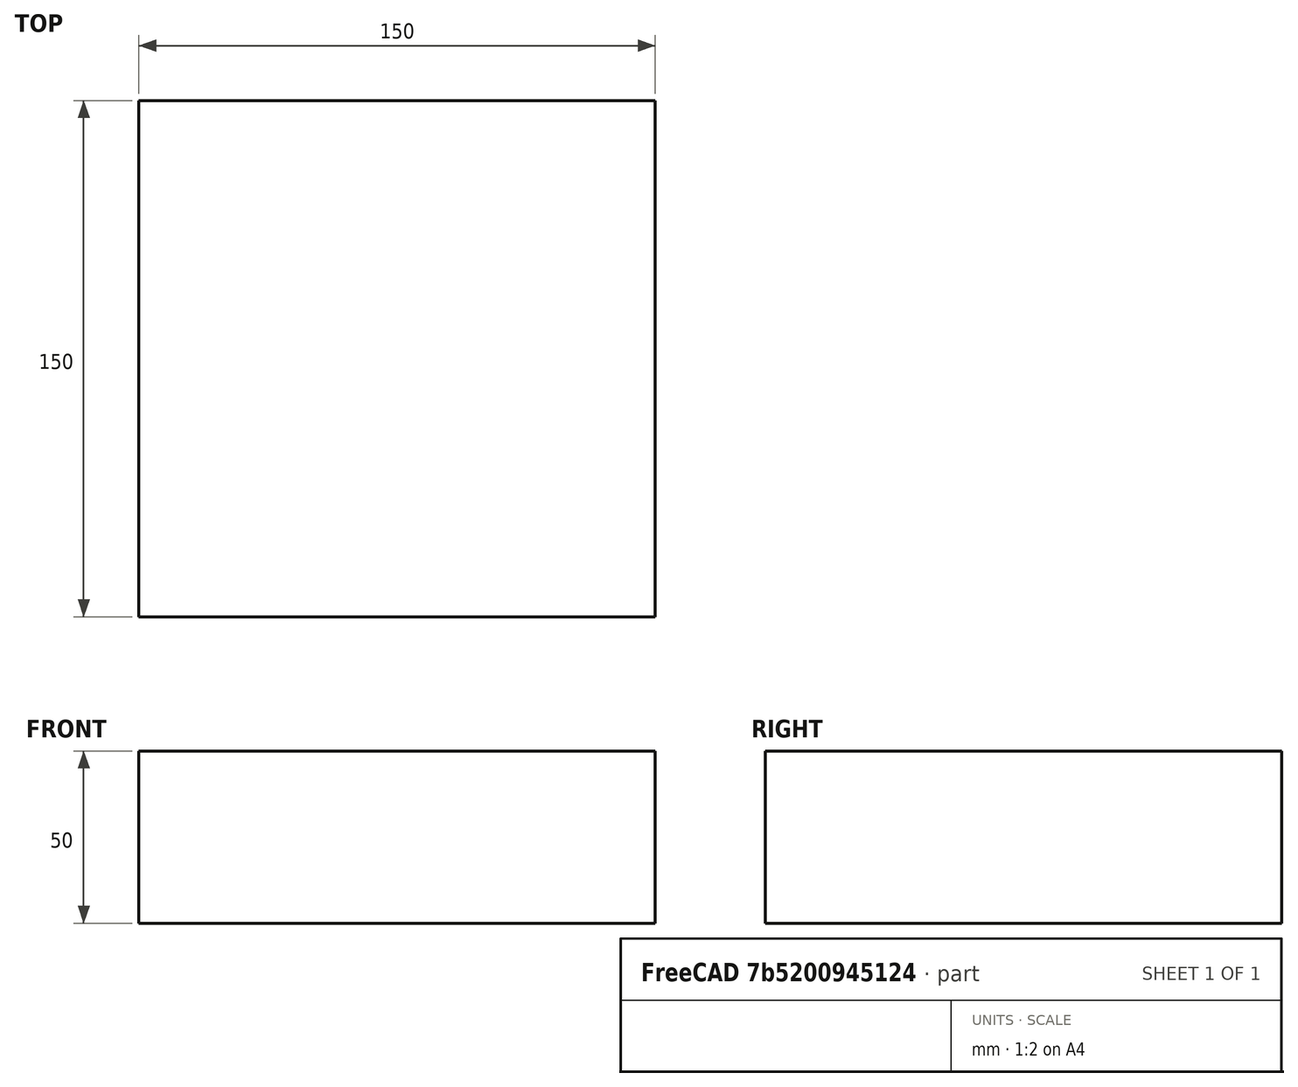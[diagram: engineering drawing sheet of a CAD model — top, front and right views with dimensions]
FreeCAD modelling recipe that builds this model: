
FCSTD DOCUMENT  (FreeCAD 0.15R4671 (Git))
Label: Square Bar 150 EN10059 S235JR
License: All rights reserved
LicenseURL: http://en.wikipedia.org/wiki/All_rights_reserved
objects: Sketcher::SketchObject×1, Part::Extrusion×1
note: 2 computed .brp shape members not serialized (recipe doc carries the construction recipe); baked Part::Feature solids carry a one-line shape summary decoded from their .brp

FEATURE [Sketcher::SketchObject] Sketch
  sketch-geometry (4):
    g0: LineSegment StartX=-75 StartY=-75 StartZ=0 EndX=75 EndY=-75 EndZ=0
    g1: LineSegment StartX=75 StartY=-75 StartZ=0 EndX=75 EndY=75 EndZ=0
    g2: LineSegment StartX=75 StartY=75 StartZ=0 EndX=-75 EndY=75 EndZ=0
    g3: LineSegment StartX=-75 StartY=75 StartZ=0 EndX=-75 EndY=-75 EndZ=0
  constraints (12):
    c: Coincident(g0,g1)
    c: Coincident(g1,g2)
    c: Coincident(g2,g3)
    c: Coincident(g3,g0)
    c: Horizontal(g0)
    c: Horizontal(g2)
    c: Vertical(g1)
    c: Vertical(g3)
    c: Symmetric(g1,g0,g-1)
    c: Symmetric(g2,g1,g-2)
    c: Equal(g1,g2)
    c: DistanceY(g1) = 150
FEATURE [Part::Extrusion] Extrude  label="Square Bar 150 EN10059 S235JR"
  Base = -> Sketch
  Dir = (0,0,50)
  Solid = true
